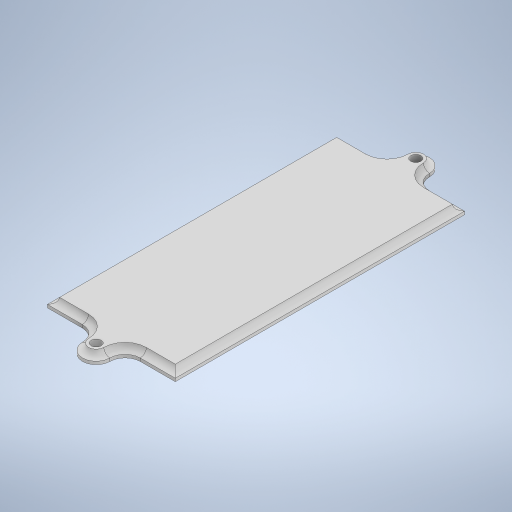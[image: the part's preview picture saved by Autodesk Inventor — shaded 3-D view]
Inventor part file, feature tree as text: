
AUTODESK INVENTOR PART (.ipt)
format: ipt  version: 2024.2 (Build 282272000, 272)  size: 279,552 bytes
history: native  units: in
note: dims shown in document units (in); Inventor stores cm internally (conversion verified against a paired STEP export)
features: extrude x1, fillet x1, sketch x1
ambient origin geometry x8: Origin, YZ Plane, XZ Plane, XY Plane, X Axis, Y Axis, Z Axis, Center Point
bodies: Solid1 (feature_tree)
feature tree (3):
  extrude  "Extrusion1"  Depth=0.0787in
  fillet  "Fillet1"  Radius=3.7402in
  sketch  "Sketch1"  dims[d0=0.1969in d1=1.6535in d2=3.7402in d3=0.1299in d4=0.8268in d5=0.1299in d6=0.1969in d7=0.8268in d8=0.3543in d9=0.1969in d10=0.1181in d11=0.0in d12=0.0787in]
